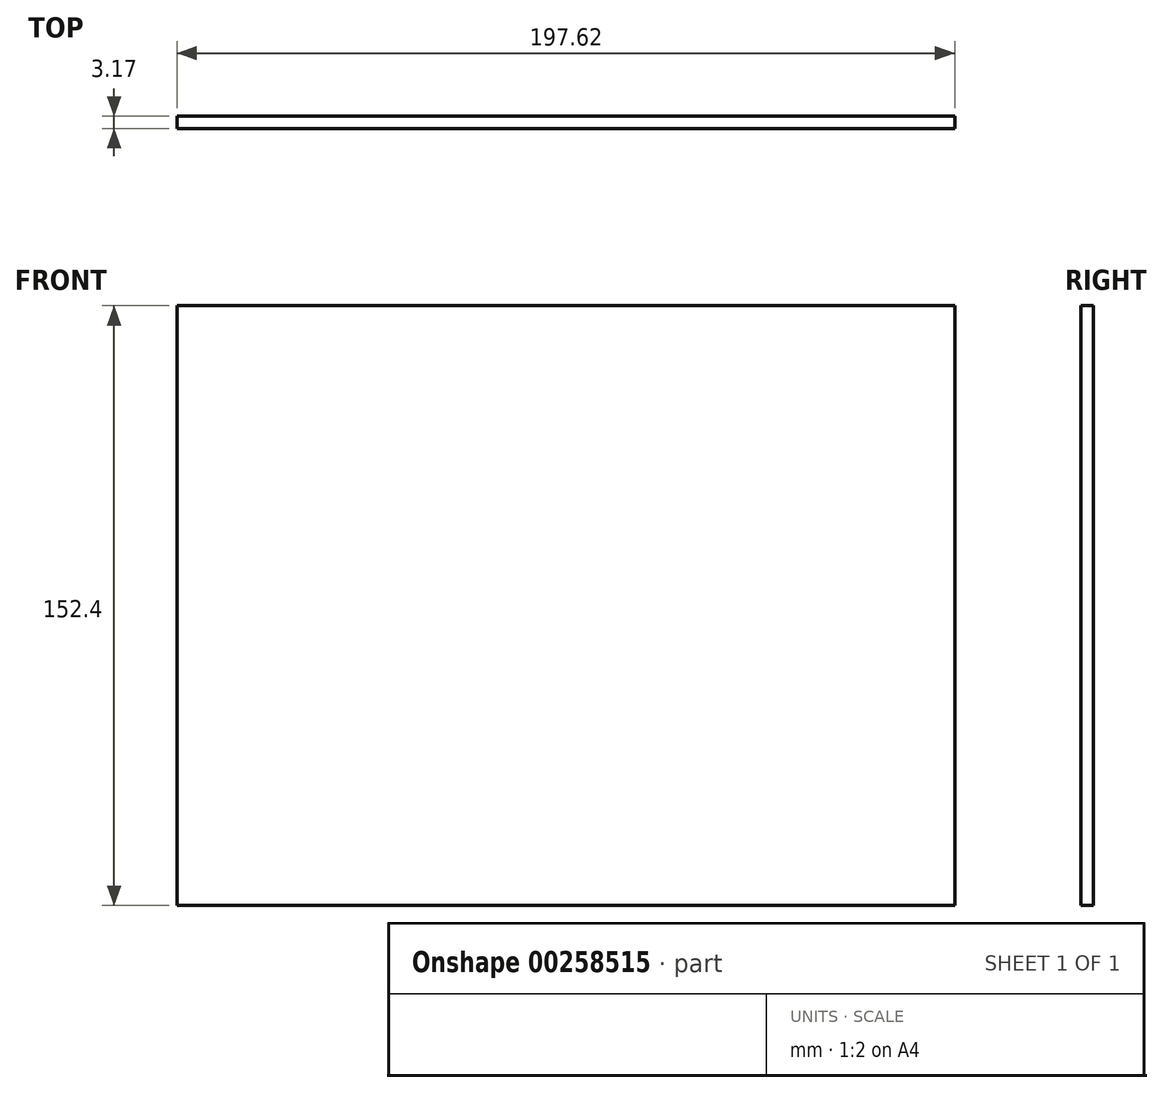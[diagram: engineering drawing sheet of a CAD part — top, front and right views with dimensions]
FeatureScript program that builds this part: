
annotation { "Feature Type Name" : "Feature", "Feature Type Description" : "" }
export const myFeature = defineFeature(function(context is Context, id is Id, definition is map)
    precondition{}
    {
        {
            var Q0;
            Q0=qCreatedBy(makeId("Front.planeOp"),FACE);
            var sketch = newSketch(context, id + "F0", { "sketchPlane" : qUnion([Q0])});
            skLineSegment(sketch, "E0.bottom", {"start": v(98.8, 76.2) * mm, "end": v(-98.8, 76.2) * mm});
            skLineSegment(sketch, "E0.top", {"start": v(98.8, -76.2) * mm, "end": v(-98.8, -76.2) * mm});
            skLineSegment(sketch, "E0.left", {"start": v(98.8, 76.2) * mm, "end": v(98.8, -76.2) * mm});
            skLineSegment(sketch, "E0.right", {"start": v(-98.8, 76.2) * mm, "end": v(-98.8, -76.2) * mm});
            skPoint(sketch, "E0.middle", {"position": v(0, 0) * mm});
            skSolve(sketch);
        }
        {
            var Q0;
            Q0 = qSketchRegion(id + "F0", true);
            extrude(context, id + "F1", {"entities" : qUnion([Q0]), "depth" : 3.17 * mm});
        }
    });
